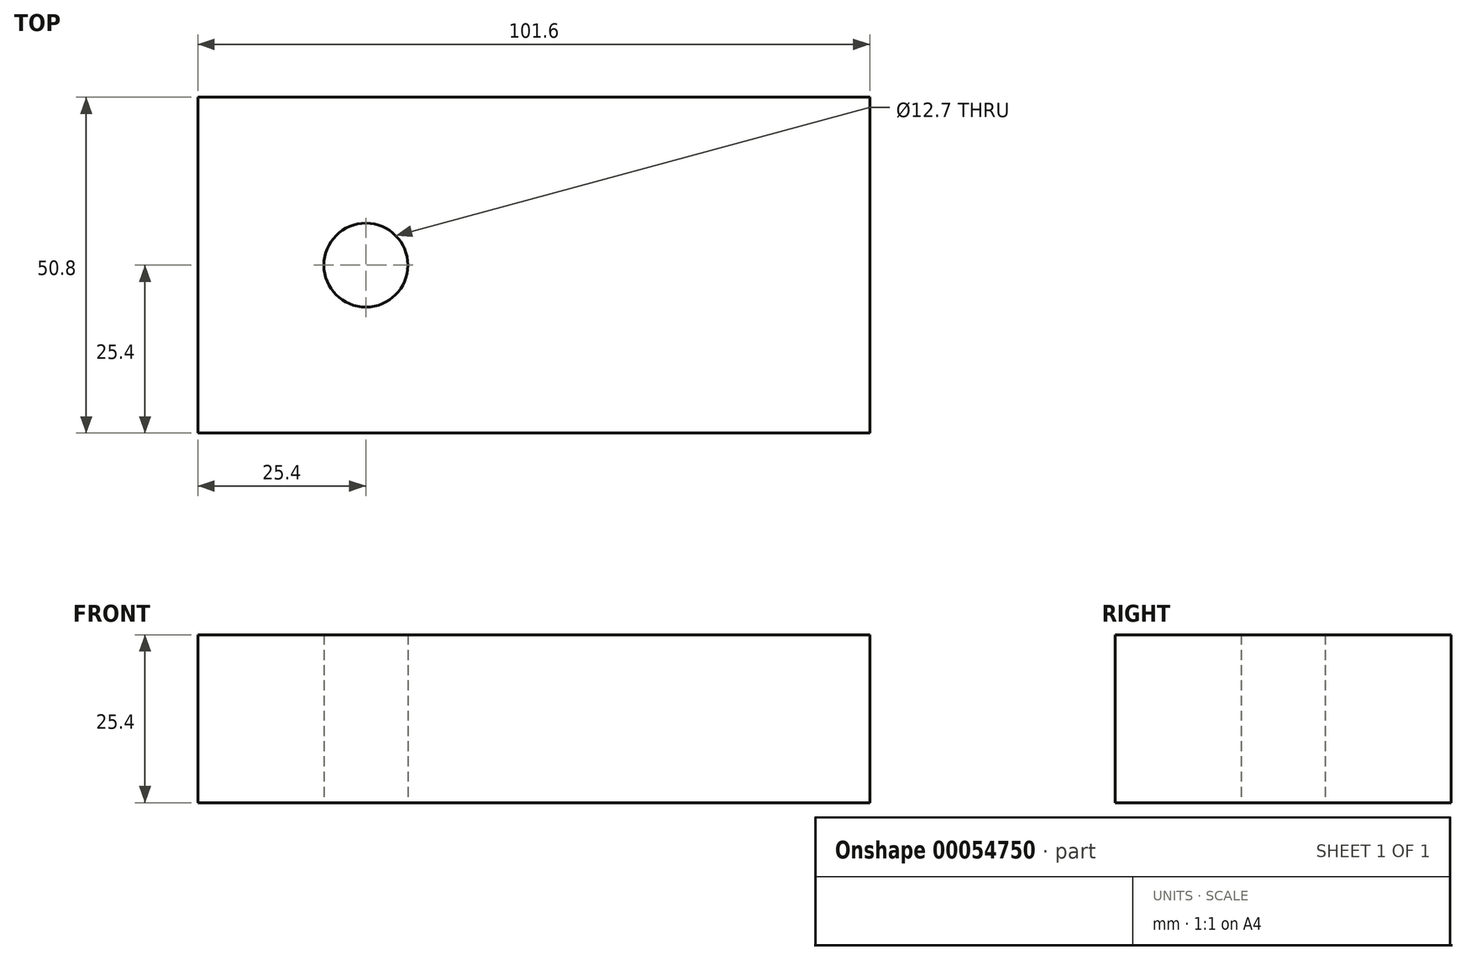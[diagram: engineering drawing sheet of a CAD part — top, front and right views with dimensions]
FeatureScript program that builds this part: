
annotation { "Feature Type Name" : "Feature", "Feature Type Description" : "" }
export const myFeature = defineFeature(function(context is Context, id is Id, definition is map)
    precondition{}
    {
        {
            var Q0;
            Q0=qCreatedBy(makeId("Top.planeOp"),FACE);
            var sketch = newSketch(context, id + "F0", { "sketchPlane" : qUnion([Q0])});
            skLineSegment(sketch, "E0.bottom", {"start": v(-75.7, 25.4) * mm, "end": v(25.9, 25.4) * mm});
            skLineSegment(sketch, "E0.top", {"start": v(-75.7, -25.4) * mm, "end": v(25.9, -25.4) * mm});
            skLineSegment(sketch, "E0.left", {"start": v(-75.7, 25.4) * mm, "end": v(-75.7, -25.4) * mm});
            skLineSegment(sketch, "E0.right", {"start": v(25.9, 25.4) * mm, "end": v(25.9, -25.4) * mm});
            skCircle(sketch, "E1", {"center": v(-50.3, 0) * mm, "radius": 6.35 * mm});
            skSolve(sketch);
        }
        {
            var Q0;
            Q0=makeQuery(id+"F0.imprint","IMPRINT",FACE,{"disambiguationData":[TD([[makeQuery(id+"F0.imprint","IMPRINT",EDGE,{"derivedFrom":sQuery(id+"F0.wireOp",EDGE,"E0.bottom")}),-1.0]])]});
            extrude(context, id + "F1", {"entities" : qUnion([Q0]), "depth" : 25.4 * mm});
        }
    });
